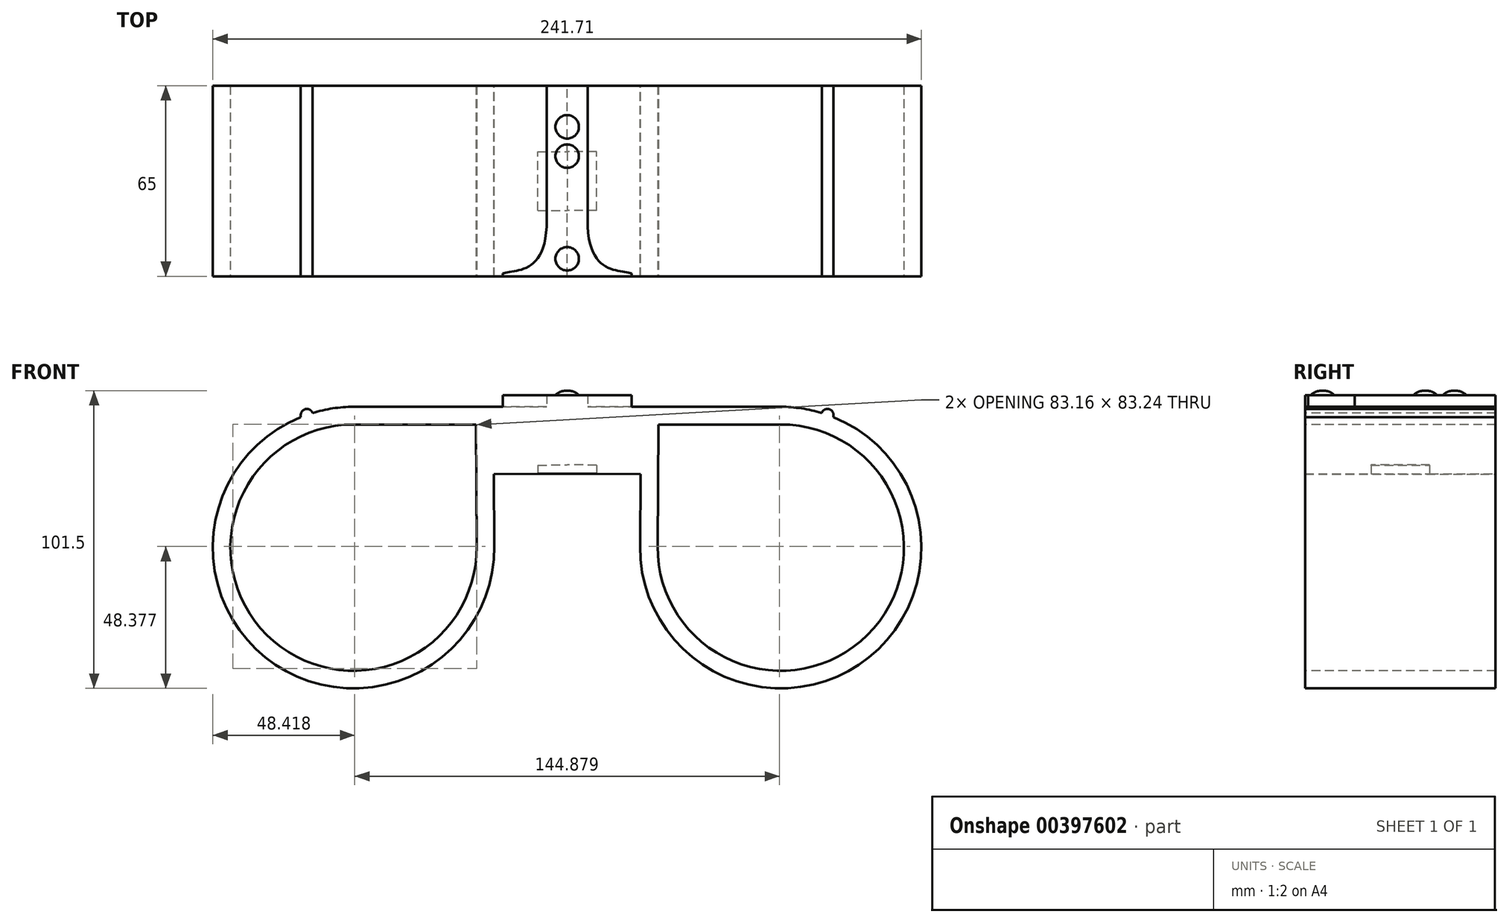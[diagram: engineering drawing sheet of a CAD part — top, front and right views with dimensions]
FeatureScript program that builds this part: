
annotation { "Feature Type Name" : "Feature", "Feature Type Description" : "" }
export const myFeature = defineFeature(function(context is Context, id is Id, definition is map)
    precondition{}
    {
        {
            var Q0;
            Q0=qCreatedBy(makeId("Front.planeOp"),FACE);
            var sketch = newSketch(context, id + "F0", { "sketchPlane" : qUnion([Q0])});
            skLineSegment(sketch, "E0", {"start": v(42.77, 0.25) * mm, "end": v(42.77, 23.06) * mm});
            skLineSegment(sketch, "E1", {"start": v(42.77, 23.06) * mm, "end": v(-30.09, 23.06) * mm});
            skLineSegment(sketch, "E2", {"start": v(-30.09, 23.06) * mm, "end": v(-30.09, -24.94) * mm});
            skLineSegment(sketch, "E3", {"start": v(0, 0) * mm, "end": v(17.77, 0.1) * mm});
            skCircle(sketch, "E4", {"center": v(-30.09, -24.94) * mm, "radius": 48 * mm});
            skLineSegment(sketch, "E5", {"start": v(17.91, -24.83) * mm, "end": v(17.77, 0.12) * mm});
            skPoint(sketch, "E5.endSnap0", {"position": v(21.38, 0.12) * mm});
            skLineSegment(sketch, "E6", {"start": v(17.77, 0.1) * mm, "end": v(42.77, 0.25) * mm});
            skSolve(sketch);
        }
        {
            var Q0;
            Q0=qSketchRegion(id+"F0",true);
            extrude(context, id + "F1", {"entities" : qUnion([Q0]), "depth" : 65 * mm});
        }
        {
            var Q0;
            Q0=makeQuery(id+"F1.opExtrude","CAP_FACE",FACE,{"disambiguationData":[OSD([sQuery(id+"F0.wireOp",EDGE,"E0"),sQuery(id+"F0.wireOp",EDGE,"E1"),sQuery(id+"F0.wireOp",EDGE,"E4"),sQuery(id+"F0.wireOp",EDGE,"E5"),sQuery(id+"F0.wireOp",EDGE,"E6")])],"isStart":false});
            var sketch = newSketch(context, id + "F2", { "sketchPlane" : qUnion([Q0])});
            skCircle(sketch, "E7", {"center": v(-30.09, -24.94) * mm, "radius": 48 * mm});
            skPoint(sketch, "E7.first.point", {"position": v(-58.46, 13.77) * mm});
            skPoint(sketch, "E7.second.point", {"position": v(2.11, -60.54) * mm});
            skPoint(sketch, "E7.third.point", {"position": v(-63.88, -59.04) * mm});
            skLineSegment(sketch, "E8", {"start": v(-30.09, -24.94) * mm, "end": v(-30.09, 32.11) * mm, "construction": true});
            skLineSegment(sketch, "E9", {"start": v(-30.09, -24.94) * mm, "end": v(-44.09, -24.94) * mm});
            skLineSegment(sketch, "E10", {"start": v(-44.09, -24.94) * mm, "end": v(-44.09, 50.31) * mm});
            skLineSegment(sketch, "E11", {"start": v(-44.09, -24.94) * mm, "end": v(-48.09, -24.94) * mm});
            skLineSegment(sketch, "E12", {"start": v(-48.09, -24.94) * mm, "end": v(-48.09, 37.37) * mm});
            skCircle(sketch, "E13", {"center": v(-30.09, -24.94) * mm, "radius": 50 * mm});
            skSolve(sketch);
        }
        {
            var Q0;
            {var subQ0=sQuery(id+"F2.wireOp",EDGE,"E10");var subQ1=sQuery(id+"F2.wireOp",EDGE,"E7");var subQ2=makeQuery(id+"F2.imprint","INTERSECT",VERTEX,{"derivedFrom":[subQ1,subQ0]});Q0=makeQuery(id+"F2.imprint","IMPRINT",FACE,{"disambiguationData":[TD([[makeQuery(id+"F2.imprint","IMPRINT",EDGE,{"disambiguationData":[TD([[subQ2,-1.0]])],"derivedFrom":subQ1}),-1.0]])]});}
            extrude(context, id + "F3", {"entities" : qUnion([Q0]), "operationType" : NewBodyOperationType.ADD, "oppositeDirection" : true, "depth" : 65 * mm});
        }
        {
            var Q0;
            Q0=makeQuery(id+"F3.opExtrude","SWEPT_EDGE",EDGE,{"disambiguationData":[OSD([sQuery(id+"F2.wireOp",EDGE,"E10"),sQuery(id+"F2.wireOp",EDGE,"E13")])]});
            var Q1;
            Q1=makeQuery(id+"F3.opExtrude","SWEPT_EDGE",EDGE,{"disambiguationData":[OSD([sQuery(id+"F2.wireOp",EDGE,"E12"),sQuery(id+"F2.wireOp",EDGE,"E13")])]});
            fillet(context, id + "F4", {"entities" : qUnion([Q0, Q1]), "radius" : 2 * mm, "tangentPropagation" : true, "allowEdgeOverflow" : false});
        }
        {
            var Q0;
            Q0=makeQuery(id+"F1.opExtrude","SWEPT_FACE",FACE,{"disambiguationData":[OSD([sQuery(id+"F0.wireOp",EDGE,"E6")])]});
            var sketch = newSketch(context, id + "F5", { "sketchPlane" : qUnion([Q0])});
            skLineSegment(sketch, "E14.bottom", {"start": v(32.77, 42.5) * mm, "end": v(52.77, 42.5) * mm});
            skLineSegment(sketch, "E14.top", {"start": v(32.77, 22.5) * mm, "end": v(52.77, 22.5) * mm});
            skLineSegment(sketch, "E14.left", {"start": v(32.77, 42.5) * mm, "end": v(32.77, 22.5) * mm});
            skLineSegment(sketch, "E14.right", {"start": v(52.77, 42.5) * mm, "end": v(52.77, 22.5) * mm});
            skPoint(sketch, "E14.middle", {"position": v(42.77, 32.5) * mm});
            skSolve(sketch);
        }
        {
            var Q0;
            Q0=qSketchRegion(id+"F5",true);
            extrude(context, id + "F6", {"entities" : qUnion([Q0]), "operationType" : NewBodyOperationType.REMOVE, "oppositeDirection" : true, "depth" : 3 * mm});
        }
        {
            var Q0;
            {var subQ0=sQuery(id+"F2.wireOp",EDGE,"E13");var subQ1=sQuery(id+"F2.wireOp",EDGE,"E12");var subQ2=sQuery(id+"F2.wireOp",EDGE,"E10");var subQ3=sQuery(id+"F2.wireOp",EDGE,"E7");Q0=makeQuery(id+"FzD17S7ChQ9cvDI_1.26.F3.boolean.opBoolean","MERGE",FACE,{"derivedFrom":[makeQuery(id+"FzD17S7ChQ9cvDI_1.25.F3.boolean.opBoolean","MERGE",FACE,{"derivedFrom":[makeQuery(id+"FzD17S7ChQ9cvDI_1.24.F3.boolean.opBoolean","MERGE",FACE,{"derivedFrom":[makeQuery(id+"FzD17S7ChQ9cvDI_1.23.F3.boolean.opBoolean","MERGE",FACE,{"derivedFrom":[makeQuery(id+"FzD17S7ChQ9cvDI_1.22.F3.boolean.opBoolean","MERGE",FACE,{"derivedFrom":[makeQuery(id+"FzD17S7ChQ9cvDI_1.21.F3.boolean.opBoolean","MERGE",FACE,{"derivedFrom":[makeQuery(id+"FzD17S7ChQ9cvDI_1.20.F3.boolean.opBoolean","MERGE",FACE,{"derivedFrom":[makeQuery(id+"FzD17S7ChQ9cvDI_1.19.F3.boolean.opBoolean","MERGE",FACE,{"derivedFrom":[makeQuery(id+"FzD17S7ChQ9cvDI_1.18.F3.boolean.opBoolean","MERGE",FACE,{"derivedFrom":[makeQuery(id+"FzD17S7ChQ9cvDI_1.17.F3.boolean.opBoolean","MERGE",FACE,{"derivedFrom":[makeQuery(id+"FzD17S7ChQ9cvDI_1.16.F3.boolean.opBoolean","MERGE",FACE,{"derivedFrom":[makeQuery(id+"FzD17S7ChQ9cvDI_1.15.F3.boolean.opBoolean","MERGE",FACE,{"derivedFrom":[makeQuery(id+"FzD17S7ChQ9cvDI_1.14.F3.boolean.opBoolean","MERGE",FACE,{"derivedFrom":[makeQuery(id+"FzD17S7ChQ9cvDI_1.13.F3.boolean.opBoolean","MERGE",FACE,{"derivedFrom":[makeQuery(id+"FzD17S7ChQ9cvDI_1.12.F3.boolean.opBoolean","MERGE",FACE,{"derivedFrom":[makeQuery(id+"FzD17S7ChQ9cvDI_1.11.F3.boolean.opBoolean","MERGE",FACE,{"derivedFrom":[makeQuery(id+"FzD17S7ChQ9cvDI_1.10.F3.boolean.opBoolean","MERGE",FACE,{"derivedFrom":[makeQuery(id+"FzD17S7ChQ9cvDI_1.9.F3.boolean.opBoolean","MERGE",FACE,{"derivedFrom":[makeQuery(id+"FzD17S7ChQ9cvDI_1.8.F3.boolean.opBoolean","MERGE",FACE,{"derivedFrom":[makeQuery(id+"FzD17S7ChQ9cvDI_1.7.F3.boolean.opBoolean","MERGE",FACE,{"derivedFrom":[makeQuery(id+"FzD17S7ChQ9cvDI_1.6.F3.boolean.opBoolean","MERGE",FACE,{"derivedFrom":[makeQuery(id+"FzD17S7ChQ9cvDI_1.5.F3.boolean.opBoolean","MERGE",FACE,{"derivedFrom":[makeQuery(id+"FzD17S7ChQ9cvDI_1.4.F3.boolean.opBoolean","MERGE",FACE,{"derivedFrom":[makeQuery(id+"FzD17S7ChQ9cvDI_1.3.F3.boolean.opBoolean","MERGE",FACE,{"derivedFrom":[makeQuery(id+"FzD17S7ChQ9cvDI_1.2.F3.boolean.opBoolean","MERGE",FACE,{"derivedFrom":[makeQuery(id+"FzD17S7ChQ9cvDI_1.1.F3.boolean.opBoolean","MERGE",FACE,{"derivedFrom":[makeQuery(id+"F3.boolean.opBoolean","MERGE",FACE,{"derivedFrom":[makeQuery(id+"F1.opExtrude","CAP_FACE",FACE,{"disambiguationData":[OSD([sQuery(id+"F0.wireOp",EDGE,"E0"),sQuery(id+"F0.wireOp",EDGE,"E1"),sQuery(id+"F0.wireOp",EDGE,"E4"),sQuery(id+"F0.wireOp",EDGE,"E5"),sQuery(id+"F0.wireOp",EDGE,"E6")])],"isStart":false}),makeQuery(id+"F3.opExtrude","CAP_FACE",FACE,{"disambiguationData":[OSD([subQ3,subQ2,subQ1,subQ0])],"isStart":true})]}),makeQuery(id+"FzD17S7ChQ9cvDI_1.1.F3.opExtrude","CAP_FACE",FACE,{"disambiguationData":[OSD([subQ3,subQ2,subQ1,subQ0])],"isStart":true})]}),makeQuery(id+"FzD17S7ChQ9cvDI_1.2.F3.opExtrude","CAP_FACE",FACE,{"disambiguationData":[OSD([subQ3,subQ2,subQ1,subQ0])],"isStart":true})]}),makeQuery(id+"FzD17S7ChQ9cvDI_1.3.F3.opExtrude","CAP_FACE",FACE,{"disambiguationData":[OSD([subQ3,subQ2,subQ1,subQ0])],"isStart":true})]}),makeQuery(id+"FzD17S7ChQ9cvDI_1.4.F3.opExtrude","CAP_FACE",FACE,{"disambiguationData":[OSD([subQ3,subQ2,subQ1,subQ0])],"isStart":true})]}),makeQuery(id+"FzD17S7ChQ9cvDI_1.5.F3.opExtrude","CAP_FACE",FACE,{"disambiguationData":[OSD([subQ3,subQ2,subQ1,subQ0])],"isStart":true})]}),makeQuery(id+"FzD17S7ChQ9cvDI_1.6.F3.opExtrude","CAP_FACE",FACE,{"disambiguationData":[OSD([subQ3,subQ2,subQ1,subQ0])],"isStart":true})]}),makeQuery(id+"FzD17S7ChQ9cvDI_1.7.F3.opExtrude","CAP_FACE",FACE,{"disambiguationData":[OSD([subQ3,subQ2,subQ1,subQ0])],"isStart":true})]}),makeQuery(id+"FzD17S7ChQ9cvDI_1.8.F3.opExtrude","CAP_FACE",FACE,{"disambiguationData":[OSD([subQ3,subQ2,subQ1,subQ0])],"isStart":true})]}),makeQuery(id+"FzD17S7ChQ9cvDI_1.9.F3.opExtrude","CAP_FACE",FACE,{"disambiguationData":[OSD([subQ3,subQ2,subQ1,subQ0])],"isStart":true})]}),makeQuery(id+"FzD17S7ChQ9cvDI_1.10.F3.opExtrude","CAP_FACE",FACE,{"disambiguationData":[OSD([subQ3,subQ2,subQ1,subQ0])],"isStart":true})]}),makeQuery(id+"FzD17S7ChQ9cvDI_1.11.F3.opExtrude","CAP_FACE",FACE,{"disambiguationData":[OSD([subQ3,subQ2,subQ1,subQ0])],"isStart":true})]}),makeQuery(id+"FzD17S7ChQ9cvDI_1.12.F3.opExtrude","CAP_FACE",FACE,{"disambiguationData":[OSD([subQ3,subQ2,subQ1,subQ0])],"isStart":true})]}),makeQuery(id+"FzD17S7ChQ9cvDI_1.13.F3.opExtrude","CAP_FACE",FACE,{"disambiguationData":[OSD([subQ3,subQ2,subQ1,subQ0])],"isStart":true})]}),makeQuery(id+"FzD17S7ChQ9cvDI_1.14.F3.opExtrude","CAP_FACE",FACE,{"disambiguationData":[OSD([subQ3,subQ2,subQ1,subQ0])],"isStart":true})]}),makeQuery(id+"FzD17S7ChQ9cvDI_1.15.F3.opExtrude","CAP_FACE",FACE,{"disambiguationData":[OSD([subQ3,subQ2,subQ1,subQ0])],"isStart":true})]}),makeQuery(id+"FzD17S7ChQ9cvDI_1.16.F3.opExtrude","CAP_FACE",FACE,{"disambiguationData":[OSD([subQ3,subQ2,subQ1,subQ0])],"isStart":true})]}),makeQuery(id+"FzD17S7ChQ9cvDI_1.17.F3.opExtrude","CAP_FACE",FACE,{"disambiguationData":[OSD([subQ3,subQ2,subQ1,subQ0])],"isStart":true})]}),makeQuery(id+"FzD17S7ChQ9cvDI_1.18.F3.opExtrude","CAP_FACE",FACE,{"disambiguationData":[OSD([subQ3,subQ2,subQ1,subQ0])],"isStart":true})]}),makeQuery(id+"FzD17S7ChQ9cvDI_1.19.F3.opExtrude","CAP_FACE",FACE,{"disambiguationData":[OSD([subQ3,subQ2,subQ1,subQ0])],"isStart":true})]}),makeQuery(id+"FzD17S7ChQ9cvDI_1.20.F3.opExtrude","CAP_FACE",FACE,{"disambiguationData":[OSD([subQ3,subQ2,subQ1,subQ0])],"isStart":true})]}),makeQuery(id+"FzD17S7ChQ9cvDI_1.21.F3.opExtrude","CAP_FACE",FACE,{"disambiguationData":[OSD([subQ3,subQ2,subQ1,subQ0])],"isStart":true})]}),makeQuery(id+"FzD17S7ChQ9cvDI_1.22.F3.opExtrude","CAP_FACE",FACE,{"disambiguationData":[OSD([subQ3,subQ2,subQ1,subQ0])],"isStart":true})]}),makeQuery(id+"FzD17S7ChQ9cvDI_1.23.F3.opExtrude","CAP_FACE",FACE,{"disambiguationData":[OSD([subQ3,subQ2,subQ1,subQ0])],"isStart":true})]}),makeQuery(id+"FzD17S7ChQ9cvDI_1.24.F3.opExtrude","CAP_FACE",FACE,{"disambiguationData":[OSD([subQ3,subQ2,subQ1,subQ0])],"isStart":true})]}),makeQuery(id+"FzD17S7ChQ9cvDI_1.25.F3.opExtrude","CAP_FACE",FACE,{"disambiguationData":[OSD([subQ3,subQ2,subQ1,subQ0])],"isStart":true})]}),makeQuery(id+"FzD17S7ChQ9cvDI_1.26.F3.opExtrude","CAP_FACE",FACE,{"disambiguationData":[OSD([subQ3,subQ2,subQ1,subQ0])],"isStart":true})]});}
            var sketch = newSketch(context, id + "F7", { "sketchPlane" : qUnion([Q0])});
            skCircle(sketch, "E15", {"center": v(-30.09, -24.94) * mm, "radius": 48 * mm});
            skPoint(sketch, "E15.first.point", {"position": v(-61.66, 11.21) * mm});
            skPoint(sketch, "E15.second.point", {"position": v(2.56, -60.13) * mm});
            skPoint(sketch, "E15.third.point", {"position": v(-63.24, -59.66) * mm});
            skArc(sketch, "E16.0", {"start": v(-5.97, -59.33) * mm, "mid": v(-3.45, -57.41) * mm, "end": v(-1.07, -55.3) * mm});
            skArc(sketch, "E16.1", {"start": v(-11.42, -62.57) * mm, "mid": v(-8.64, -61.05) * mm, "end": v(-5.97, -59.33) * mm});
            skArc(sketch, "E16.2", {"start": v(-17.3, -64.95) * mm, "mid": v(-14.31, -63.87) * mm, "end": v(-11.42, -62.57) * mm});
            skArc(sketch, "E16.3", {"start": v(-23.46, -66.42) * mm, "mid": v(-20.35, -65.8) * mm, "end": v(-17.3, -64.95) * mm});
            skArc(sketch, "E16.4", {"start": v(-29.78, -66.94) * mm, "mid": v(-26.6, -66.8) * mm, "end": v(-23.46, -66.42) * mm});
            skArc(sketch, "E16.5", {"start": v(-36.1, -66.51) * mm, "mid": v(-32.95, -66.85) * mm, "end": v(-29.78, -66.94) * mm});
            skArc(sketch, "E16.6", {"start": v(-42.29, -65.13) * mm, "mid": v(-39.22, -65.94) * mm, "end": v(-36.1, -66.51) * mm});
            skArc(sketch, "E16.7", {"start": v(-62.55, 1.7) * mm, "mid": v(-64.47, -0.82) * mm, "end": v(-66.2, -3.48) * mm});
            skArc(sketch, "E16.8", {"start": v(-58.17, 6.29) * mm, "mid": v(-60.45, 4.08) * mm, "end": v(-62.55, 1.7) * mm});
            skArc(sketch, "E16.9", {"start": v(-53.15, 10.16) * mm, "mid": v(-55.74, 8.32) * mm, "end": v(-58.17, 6.29) * mm});
            skArc(sketch, "E16.10", {"start": v(-47.61, 13.23) * mm, "mid": v(-50.44, 11.8) * mm, "end": v(-53.15, 10.16) * mm});
            skArc(sketch, "E16.11", {"start": v(-41.67, 15.43) * mm, "mid": v(-44.68, 14.44) * mm, "end": v(-47.61, 13.23) * mm});
            skArc(sketch, "E16.12", {"start": v(-35.46, 16.71) * mm, "mid": v(-38.59, 16.19) * mm, "end": v(-41.67, 15.43) * mm});
            skArc(sketch, "E16.13", {"start": v(3.16, -50.6) * mm, "mid": v(9.73, -38.31) * mm, "end": v(11.9, -24.55) * mm});
            skLineSegment(sketch, "E16.14", {"start": v(11.9, -24.55) * mm, "end": v(11.67, 17.06) * mm});
            skLineSegment(sketch, "E16.15", {"start": v(11.67, 17.06) * mm, "end": v(-30.09, 17.06) * mm});
            skArc(sketch, "E16.16", {"start": v(-30.09, 17.06) * mm, "mid": v(-32.78, 16.97) * mm, "end": v(-35.46, 16.71) * mm});
            skArc(sketch, "E16.17", {"start": v(-66.2, -3.48) * mm, "mid": v(-67.7, -6.27) * mm, "end": v(-69, -9.16) * mm});
            skArc(sketch, "E16.18", {"start": v(-69, -9.16) * mm, "mid": v(-70.09, -12.14) * mm, "end": v(-70.94, -15.2) * mm});
            skArc(sketch, "E16.19", {"start": v(-70.94, -15.2) * mm, "mid": v(-71.56, -18.3) * mm, "end": v(-71.94, -21.45) * mm});
            skArc(sketch, "E16.20", {"start": v(-71.94, -21.45) * mm, "mid": v(-72.09, -24.62) * mm, "end": v(-72, -27.79) * mm});
            skArc(sketch, "E16.21", {"start": v(-72, -27.79) * mm, "mid": v(-71.66, -30.94) * mm, "end": v(-71.09, -34.06) * mm});
            skArc(sketch, "E16.22", {"start": v(-71.09, -34.06) * mm, "mid": v(-70.28, -37.13) * mm, "end": v(-69.25, -40.13) * mm});
            skArc(sketch, "E16.23", {"start": v(-69.25, -40.13) * mm, "mid": v(-68, -43.04) * mm, "end": v(-66.52, -45.85) * mm});
            skArc(sketch, "E16.24", {"start": v(-1.07, -55.3) * mm, "mid": v(1.13, -53.03) * mm, "end": v(3.16, -50.6) * mm});
            skArc(sketch, "E16.25", {"start": v(-66.52, -45.85) * mm, "mid": v(-64.84, -48.54) * mm, "end": v(-62.96, -51.09) * mm});
            skArc(sketch, "E16.26", {"start": v(-62.96, -51.09) * mm, "mid": v(-60.9, -53.5) * mm, "end": v(-58.65, -55.74) * mm});
            skArc(sketch, "E16.27", {"start": v(-58.65, -55.74) * mm, "mid": v(-56.24, -57.8) * mm, "end": v(-53.7, -59.68) * mm});
            skArc(sketch, "E16.28", {"start": v(-53.7, -59.68) * mm, "mid": v(-51, -61.37) * mm, "end": v(-48.2, -62.84) * mm});
            skArc(sketch, "E16.29", {"start": v(-48.2, -62.84) * mm, "mid": v(-45.28, -64.1) * mm, "end": v(-42.29, -65.13) * mm});
            skSolve(sketch);
        }
        {
            var Q0;
            Q0=makeQuery(id+"F7.imprint","IMPRINT",FACE,{"disambiguationData":[TD([[makeQuery(id+"F7.imprint","IMPRINT",EDGE,{"derivedFrom":sQuery(id+"F7.wireOp",EDGE,"E16.0")}),1.0]])]});
            var Q1;
            {var subQ0=sQuery(id+"F7.wireOp",EDGE,"E16.14");var subQ1=sQuery(id+"F7.wireOp",EDGE,"E15");var subQ2=makeQuery(id+"F7.imprint","INTERSECT",VERTEX,{"derivedFrom":[subQ1,subQ0]});Q1=makeQuery(id+"F7.imprint","IMPRINT",FACE,{"disambiguationData":[TD([[makeQuery(id+"F7.imprint","IMPRINT",EDGE,{"disambiguationData":[TD([[subQ2,-1.0]])],"derivedFrom":subQ1}),-1.0]])]});}
            extrude(context, id + "F8", {"entities" : qUnion([Q0, Q1]), "operationType" : NewBodyOperationType.REMOVE, "oppositeDirection" : true, "depth" : 75 * mm});
        }
        {
            var Q0;
            Q0=makeQuery(id+"F1.opExtrude","SWEPT_FACE",FACE,{"disambiguationData":[OSD([sQuery(id+"F0.wireOp",EDGE,"E1")])]});
            var sketch = newSketch(context, id + "F9", { "sketchPlane" : qUnion([Q0])});
            skLineSegment(sketch, "E17.bottom", {"start": v(42.77, -65) * mm, "end": v(20.77, -65) * mm});
            skLineSegment(sketch, "E17.top", {"start": v(42.77, -64) * mm, "end": v(20.77, -64) * mm});
            skLineSegment(sketch, "E17.left", {"start": v(42.77, -65) * mm, "end": v(42.77, -64) * mm});
            skLineSegment(sketch, "E17.right", {"start": v(20.77, -65) * mm, "end": v(20.77, -64) * mm});
            skLineSegment(sketch, "E18.bottom", {"start": v(42.77, 0) * mm, "end": v(35.77, 0) * mm});
            skLineSegment(sketch, "E18.top", {"start": v(42.77, -64) * mm, "end": v(35.77, -64) * mm});
            skLineSegment(sketch, "E18.left", {"start": v(42.77, 0) * mm, "end": v(42.77, -64) * mm});
            skLineSegment(sketch, "E18.right", {"start": v(35.77, 0) * mm, "end": v(35.77, -64) * mm});
            skFitSpline(sketch, "E19", {"points": [v(20.77, -64) * mm, v(35.77, -48.01) * mm], "startDerivative": vector(10.39, 4.39) * mm, "endDerivative": vector(2.48, 50.96) * mm});
            skSolve(sketch);
        }
        {
            var Q0;
            {var subQ1=sQuery(id+"F9.wireOp",EDGE,"E18.bottom");Q0=makeQuery(id+"F9.imprint","IMPRINT",FACE,{"disambiguationData":[TD([[makeQuery(id+"F9.imprint","IMPRINT",EDGE,{"derivedFrom":subQ1}),1.0]])]});}
            var Q1;
            {var subQ0=sQuery(id+"F9.wireOp",EDGE,"E17.top");Q1=makeQuery(id+"F9.imprint","IMPRINT",FACE,{"disambiguationData":[TD([[makeQuery(id+"F9.imprint","IMPRINT",EDGE,{"derivedFrom":subQ0}),-1.0]])]});}
            var Q2;
            Q2=makeQuery(id+"F9.imprint","IMPRINT",FACE,{"disambiguationData":[TD([[makeQuery(id+"F9.imprint","IMPRINT",EDGE,{"derivedFrom":sQuery(id+"F9.wireOp",EDGE,"E17.bottom")}),-1.0]])]});
            extrude(context, id + "F10", {"entities" : qUnion([Q0, Q1, Q2]), "operationType" : NewBodyOperationType.ADD, "depth" : 4 * mm});
        }
        {
            var Q0;
            Q0=makeQuery(id+"F1.opExtrude","SWEPT_BODY",BODY,{"disambiguationData":[OSD([sQuery(id+"F0.wireOp",EDGE,"E0"),sQuery(id+"F0.wireOp",EDGE,"E1"),sQuery(id+"F0.wireOp",EDGE,"E3"),sQuery(id+"F0.wireOp",EDGE,"E4")])]});
            var Q1;
            Q1=makeQuery(id+"F1.opExtrude","SWEPT_FACE",FACE,{"disambiguationData":[OSD([sQuery(id+"F0.wireOp",EDGE,"E0")])]});
            mirror(context, id + "F11", {"operationType" : NewBodyOperationType.ADD, "entities" : qUnion([Q0]), "mirrorPlane" : qUnion([Q1])});
        }
        {
            var Q0;
            {var subQ0=makeQuery(id+"F10.opExtrude","CAP_FACE",FACE,{"disambiguationData":[OSD([sQuery(id+"F9.wireOp",EDGE,"E17.bottom"),sQuery(id+"F9.wireOp",EDGE,"E17.left"),sQuery(id+"F9.wireOp",EDGE,"E17.right"),sQuery(id+"F9.wireOp",EDGE,"E18.bottom"),sQuery(id+"F9.wireOp",EDGE,"E18.left"),sQuery(id+"F9.wireOp",EDGE,"E18.right"),sQuery(id+"F9.wireOp",EDGE,"E19")])],"isStart":false});Q0=makeQuery(id+"F11.boolean.opBoolean","MERGE",FACE,{"derivedFrom":[subQ0,makeQuery(id+"F11.opPattern","COPY",FACE,{"derivedFrom":subQ0,"instanceName":"1"})]});}
            var sketch = newSketch(context, id + "F12", { "sketchPlane" : qUnion([Q0])});
            skLineSegment(sketch, "E20", {"start": v(42.77, -65) * mm, "end": v(42.77, -59) * mm});
            skCircle(sketch, "E21", {"center": v(42.77, -59) * mm, "radius": 4 * mm});
            skLineSegment(sketch, "E22", {"start": v(42.77, -59) * mm, "end": v(42.77, -24) * mm});
            skPoint(sketch, "E22.endSnap0", {"position": v(49.77, -24) * mm});
            skCircle(sketch, "E23", {"center": v(42.77, -24) * mm, "radius": 4 * mm});
            skLineSegment(sketch, "E24", {"start": v(42.77, -24) * mm, "end": v(42.77, -14) * mm});
            skCircle(sketch, "E25", {"center": v(42.77, -14) * mm, "radius": 4 * mm});
            skSolve(sketch);
        }
        {
            var Q0;
            Q0=qSketchRegion(id+"F12",true);
            extrude(context, id + "F13", {"entities" : qUnion([Q0]), "operationType" : NewBodyOperationType.ADD, "depth" : 1.5 * mm});
        }
        {
            var Q0;
            Q0=makeQuery(id+"F13.opExtrude","CAP_EDGE",EDGE,{"disambiguationData":[OSD([sQuery(id+"F12.wireOp",EDGE,"E21")])],"isStart":false});
            var Q1;
            Q1=makeQuery(id+"F13.opExtrude","CAP_EDGE",EDGE,{"disambiguationData":[OSD([sQuery(id+"F12.wireOp",EDGE,"E23")])],"isStart":false});
            var Q2;
            Q2=makeQuery(id+"F13.opExtrude","CAP_EDGE",EDGE,{"disambiguationData":[OSD([sQuery(id+"F12.wireOp",EDGE,"E25")])],"isStart":false});
            fillet(context, id + "F14", {"entities" : qUnion([Q0, Q1, Q2]), "radius" : 5 * mm, "tangentPropagation" : true, "allowEdgeOverflow" : false});
        }
    });
